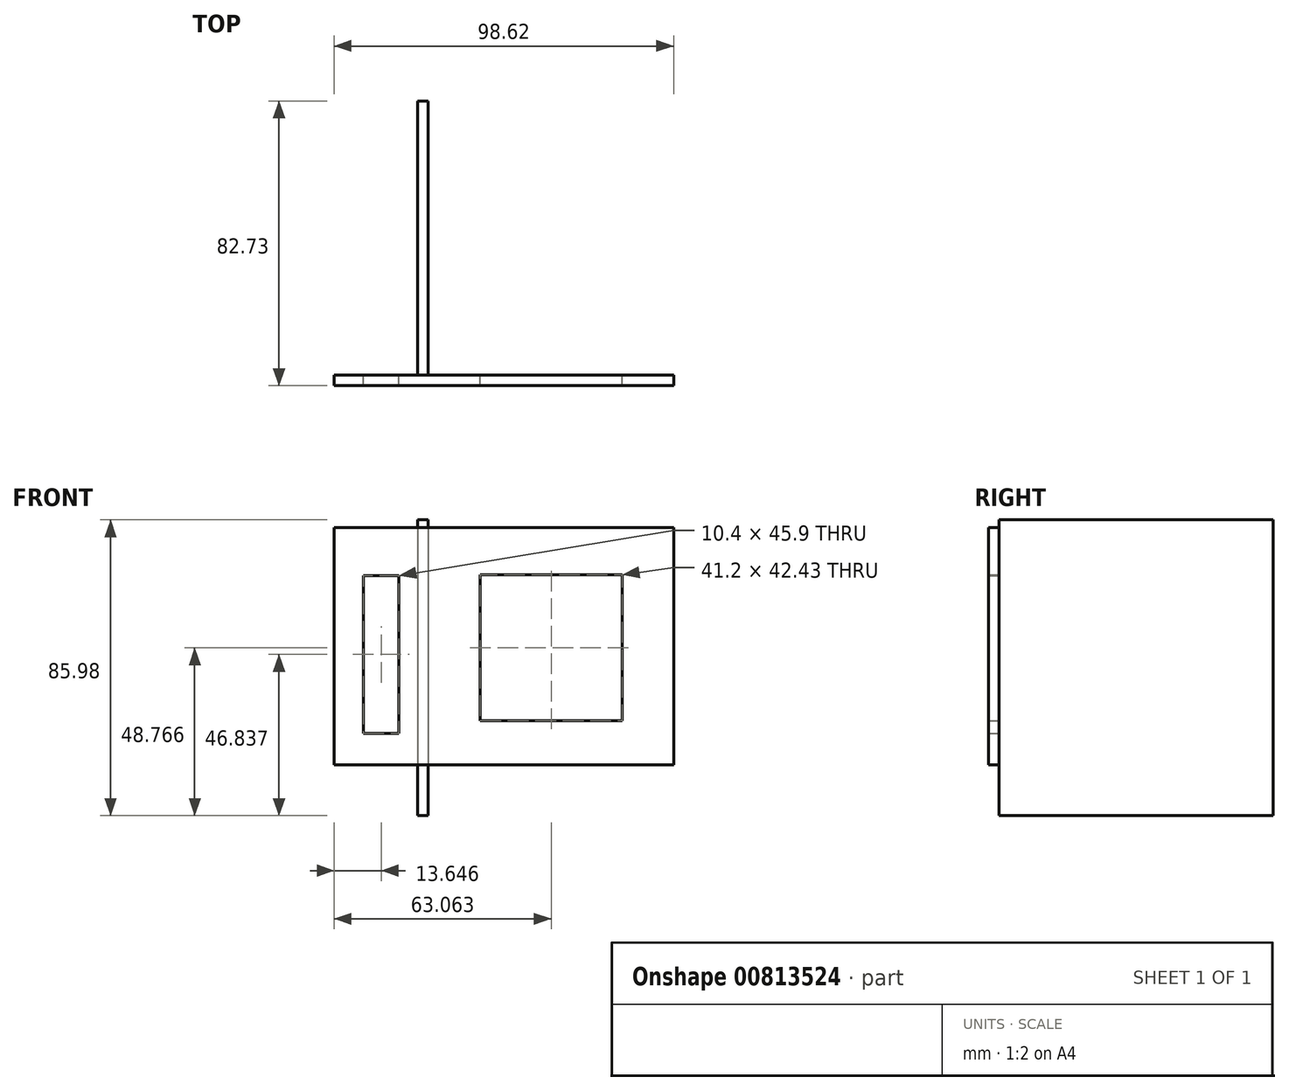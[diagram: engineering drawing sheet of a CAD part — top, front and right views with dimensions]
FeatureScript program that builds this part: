
annotation { "Feature Type Name" : "Feature", "Feature Type Description" : "" }
export const myFeature = defineFeature(function(context is Context, id is Id, definition is map)
    precondition{}
    {
        {
            var Q0;
            Q0=qCreatedBy(makeId("Right.planeOp"),FACE);
            var sketch = newSketch(context, id + "F0", { "sketchPlane" : qUnion([Q0])});
            skLineSegment(sketch, "E0.bottom", {"start": v(-32.22, 36.28) * mm, "end": v(47.51, 36.28) * mm});
            skLineSegment(sketch, "E0.top", {"start": v(-32.22, -49.7) * mm, "end": v(47.51, -49.7) * mm});
            skLineSegment(sketch, "E0.left", {"start": v(-32.22, 36.28) * mm, "end": v(-32.22, -49.7) * mm});
            skLineSegment(sketch, "E0.right", {"start": v(47.51, 36.28) * mm, "end": v(47.51, -49.7) * mm});
            skSolve(sketch);
        }
        {
            var Q0;
            Q0=qSketchRegion(id+"F0",true);
            extrude(context, id + "F1", {"entities" : qUnion([Q0]), "endBound" : BoundingType.SYMMETRIC, "depth" : 3 * mm, "offsetDistance" : 25 * mm});
        }
        {
            var Q0;
            Q0=makeQuery(id+"F1.opExtrude","SWEPT_FACE",FACE,{"disambiguationData":[OSD([sQuery(id+"F0.wireOp",EDGE,"E0.left")])]});
            var sketch = newSketch(context, id + "F2", { "sketchPlane" : qUnion([Q0])});
            skLineSegment(sketch, "E1.bottom", {"start": v(-25.76, 33.96) * mm, "end": v(72.86, 33.96) * mm});
            skLineSegment(sketch, "E1.top", {"start": v(-25.76, -34.9) * mm, "end": v(72.86, -34.9) * mm});
            skLineSegment(sketch, "E1.left", {"start": v(-25.76, 33.96) * mm, "end": v(-25.76, -34.9) * mm});
            skLineSegment(sketch, "E1.right", {"start": v(72.86, 33.96) * mm, "end": v(72.86, -34.9) * mm});
            skPoint(sketch, "E2", {"position": v(0, 15.36) * mm});
            skPoint(sketch, "E3", {"position": v(0, -20.15) * mm});
            skLineSegment(sketch, "E4.bottom", {"start": v(16.7, 20.28) * mm, "end": v(57.9, 20.28) * mm});
            skLineSegment(sketch, "E4.top", {"start": v(16.7, -22.15) * mm, "end": v(57.9, -22.15) * mm});
            skLineSegment(sketch, "E4.left", {"start": v(16.7, 20.28) * mm, "end": v(16.7, -22.15) * mm});
            skLineSegment(sketch, "E4.right", {"start": v(57.9, 20.28) * mm, "end": v(57.9, -22.15) * mm});
            skLineSegment(sketch, "E5.bottom", {"start": v(-17.31, 20.09) * mm, "end": v(-6.92, 20.09) * mm});
            skLineSegment(sketch, "E5.top", {"start": v(-17.31, -25.81) * mm, "end": v(-6.92, -25.81) * mm});
            skLineSegment(sketch, "E5.left", {"start": v(-17.31, 20.09) * mm, "end": v(-17.31, -25.81) * mm});
            skLineSegment(sketch, "E5.right", {"start": v(-6.92, 20.09) * mm, "end": v(-6.92, -25.81) * mm});
            skSolve(sketch);
        }
        {
            var Q0;
            Q0=qSketchRegion(id+"F2",true);
            extrude(context, id + "F3", {"entities" : qUnion([Q0]), "depth" : 3 * mm, "offsetDistance" : 25 * mm});
        }
    });
